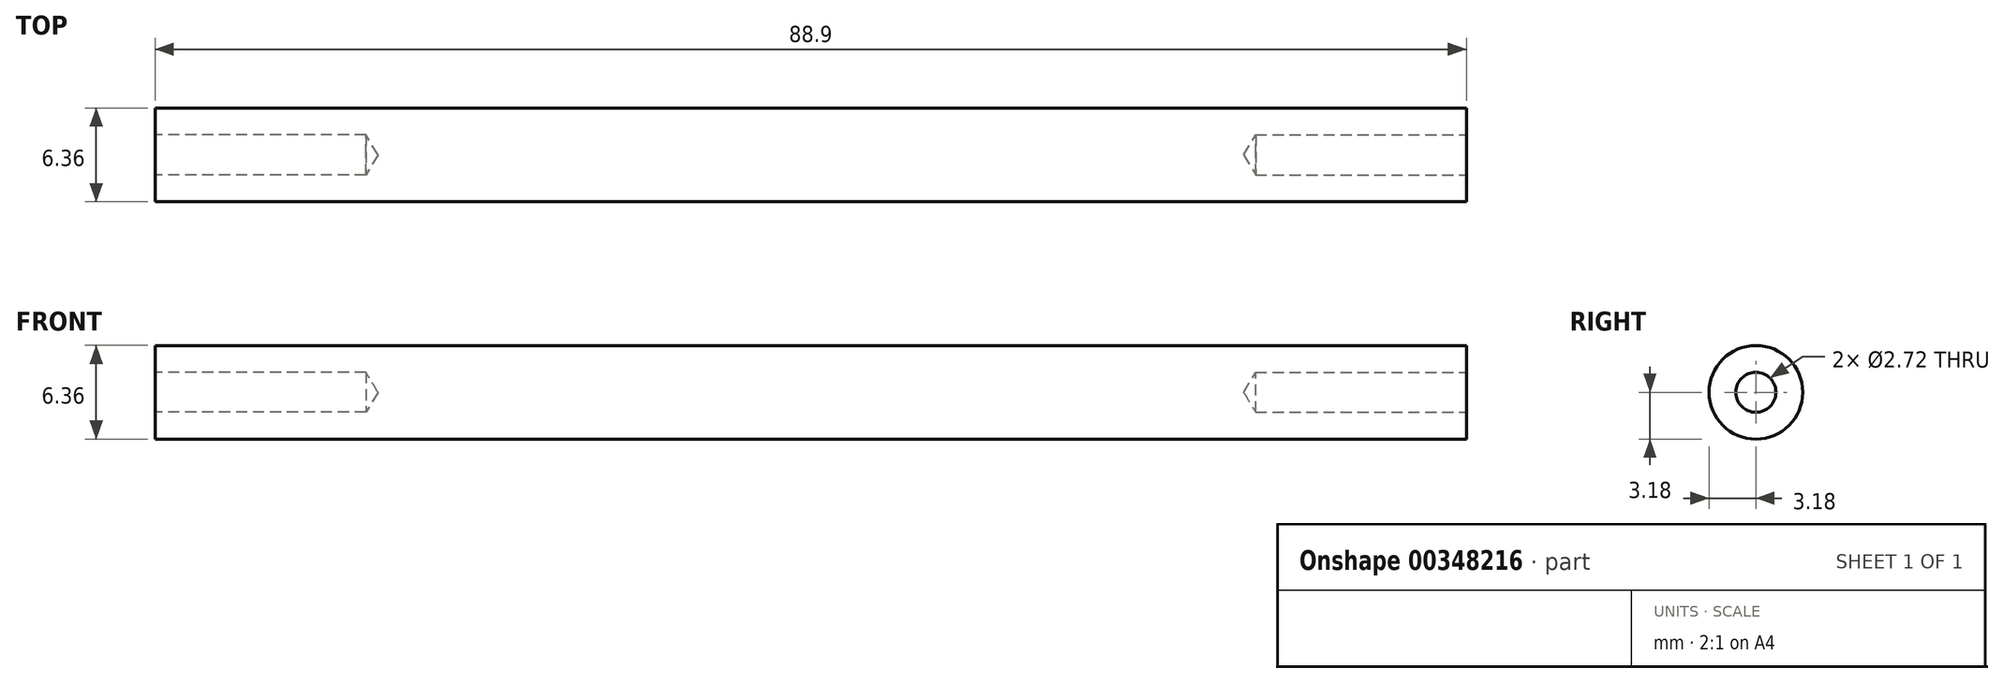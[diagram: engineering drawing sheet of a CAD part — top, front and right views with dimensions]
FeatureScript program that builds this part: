
annotation { "Feature Type Name" : "Feature", "Feature Type Description" : "" }
export const myFeature = defineFeature(function(context is Context, id is Id, definition is map)
    precondition{}
    {
        {
            var Q0;
            Q0=qCreatedBy(makeId("Right.planeOp"),FACE);
            var sketch = newSketch(context, id + "F0", { "sketchPlane" : qUnion([Q0])});
            skCircle(sketch, "E0", {"center": v(0, 0) * mm, "radius": 3.18 * mm});
            skSolve(sketch);
        }
        {
            var Q0;
            Q0=qSketchRegion(id+"F0",true);
            extrude(context, id + "F1", {"entities" : qUnion([Q0]), "endBound" : BoundingType.SYMMETRIC, "depth" : 88.9 * mm});
        }
        {
            var Q0;
            Q0=makeQuery(id+"F1.opExtrude","CAP_FACE",FACE,{"disambiguationData":[OSD([sQuery(id+"F0.wireOp",EDGE,"E0")])],"isStart":false});
            var sketch = newSketch(context, id + "F2", { "sketchPlane" : qUnion([Q0])});
            skPoint(sketch, "E1", {"position": v(0, 0) * mm});
            skSolve(sketch);
        }
        {
            var Q0;
            Q0=makeQuery(id+"F1.opExtrude","CAP_FACE",FACE,{"disambiguationData":[OSD([sQuery(id+"F0.wireOp",EDGE,"E0")])],"isStart":true});
            var sketch = newSketch(context, id + "F3", { "sketchPlane" : qUnion([Q0])});
            skPoint(sketch, "E2", {"position": v(0, 0) * mm});
            skSolve(sketch);
        }
        {
            var Q0;
            Q0=sQuery(id+"F3.wireOp",VERTEX,"E2");
            var Q1;
            Q1=sQuery(id+"F2.wireOp",VERTEX,"E1");
            var Q2;
            Q2=makeQuery(id+"F1.opExtrude","SWEPT_BODY",BODY,{"disambiguationData":[OSD([sQuery(id+"F0.wireOp",EDGE,"E0")])]});
            hole(context, id + "F4", {"style" : HoleStyle.SIMPLE, "holeDiameter" : 2.72 * mm, "endStyle" : HoleEndStyle.BLIND, "holeDepth" : 14.29 * mm, "locations" : qUnion([Q0, Q1]), "scope" : qUnion([Q2])});
        }
    });
